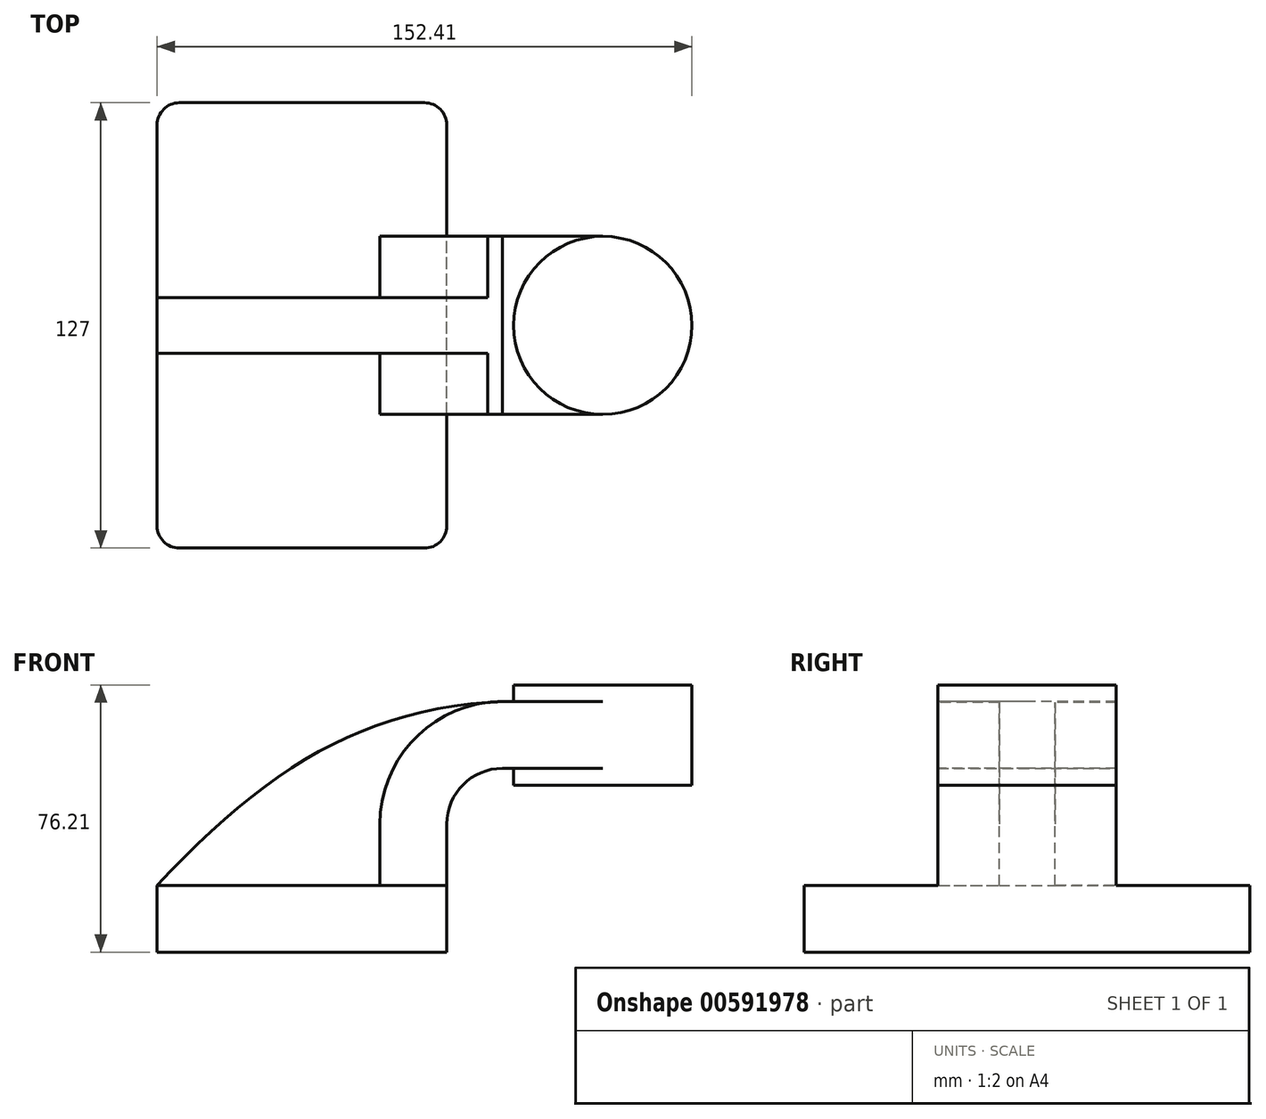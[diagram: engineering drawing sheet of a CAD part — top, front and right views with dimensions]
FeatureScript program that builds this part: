
annotation { "Feature Type Name" : "Feature", "Feature Type Description" : "" }
export const myFeature = defineFeature(function(context is Context, id is Id, definition is map)
    precondition{}
    {
        {
            var Q0;
            Q0=qCreatedBy(makeId("Front.planeOp"),FACE);
            var sketch = newSketch(context, id + "F0", { "sketchPlane" : qUnion([Q0])});
            skLineSegment(sketch, "E0.bottom", {"start": v(-41.28, -9.53) * mm, "end": v(41.28, -9.53) * mm});
            skLineSegment(sketch, "E0.top", {"start": v(-41.28, 9.52) * mm, "end": v(41.28, 9.52) * mm});
            skLineSegment(sketch, "E0.left", {"start": v(-41.28, -9.53) * mm, "end": v(-41.28, 9.52) * mm});
            skLineSegment(sketch, "E0.right", {"start": v(41.28, -9.53) * mm, "end": v(41.28, 9.52) * mm});
            skPoint(sketch, "E0.middle", {"position": v(0, 0) * mm});
            skLineSegment(sketch, "E1.bottom", {"start": v(111.12, 38.1) * mm, "end": v(60.32, 38.1) * mm});
            skLineSegment(sketch, "E1.top", {"start": v(111.12, 66.68) * mm, "end": v(60.32, 66.68) * mm});
            skLineSegment(sketch, "E1.left", {"start": v(111.12, 38.1) * mm, "end": v(111.12, 66.68) * mm});
            skLineSegment(sketch, "E1.right", {"start": v(60.32, 38.1) * mm, "end": v(60.32, 66.68) * mm});
            skPoint(sketch, "E1.middle", {"position": v(85.72, 52.39) * mm});
            skLineSegment(sketch, "E2", {"start": v(41.28, 9.52) * mm, "end": v(41.28, 27) * mm});
            skArc(sketch, "E3", {"start": v(41.28, 27) * mm, "mid": v(45.92, 38.23) * mm, "end": v(57.15, 42.88) * mm});
            skLineSegment(sketch, "E4", {"start": v(57.15, 42.88) * mm, "end": v(85.72, 42.88) * mm});
            skPoint(sketch, "E4.endSnap0", {"position": v(85.72, 38.1) * mm});
            skLineSegment(sketch, "E5.0", {"start": v(57.15, 61.93) * mm, "end": v(85.72, 61.93) * mm});
            skArc(sketch, "E5.1", {"start": v(22.23, 27) * mm, "mid": v(32.45, 51.7) * mm, "end": v(57.15, 61.93) * mm});
            skLineSegment(sketch, "E5.2", {"start": v(22.23, 9.52) * mm, "end": v(22.23, 27) * mm});
            skLineSegment(sketch, "E6", {"start": v(85.72, 38.1) * mm, "end": v(85.72, 66.68) * mm});
            skFitSpline(sketch, "E7", {"points": [v(-41.28, 9.53) * mm, v(57.15, 61.93) * mm], "startDerivative": vector(93.06, 99.37) * mm, "endDerivative": vector(120.58, 5.5) * mm});
            skSolve(sketch);
        }
        {
            var Q0;
            Q0=makeQuery(id+"F0.imprint","IMPRINT",FACE,{"disambiguationData":[TD([[makeQuery(id+"F0.imprint","IMPRINT",EDGE,{"derivedFrom":sQuery(id+"F0.wireOp",EDGE,"E0.bottom")}),1.0]])]});
            extrude(context, id + "F1", {"entities" : qUnion([Q0]), "depth" : 63.5 * mm, "offsetDistance" : 25.4 * mm});
        }
        {
            var Q0;
            {var subQ0=sQuery(id+"F0.wireOp",EDGE,"E4");var subQ1=sQuery(id+"F0.wireOp",EDGE,"E1.right");var subQ2=makeQuery(id+"F0.imprint","INTERSECT",VERTEX,{"derivedFrom":[subQ1,subQ0]});Q0=makeQuery(id+"F0.imprint","IMPRINT",FACE,{"disambiguationData":[TD([[makeQuery(id+"F0.imprint","IMPRINT",EDGE,{"disambiguationData":[TD([[subQ2,-1.0]])],"derivedFrom":subQ1}),-1.0]])]});}
            var Q1;
            {var subQ1=sQuery(id+"F0.wireOp",EDGE,"E2");Q1=makeQuery(id+"F0.imprint","IMPRINT",FACE,{"disambiguationData":[TD([[makeQuery(id+"F0.imprint","IMPRINT",EDGE,{"derivedFrom":subQ1}),1.0]])]});}
            extrude(context, id + "F2", {"entities" : qUnion([Q0, Q1]), "operationType" : NewBodyOperationType.ADD, "depth" : 25.4 * mm, "offsetDistance" : 25.4 * mm});
        }
        {
            var Q0;
            {var subQ3=sQuery(id+"F0.wireOp",EDGE,"E5.2");Q0=makeQuery(id+"F0.imprint","IMPRINT",FACE,{"disambiguationData":[TD([[makeQuery(id+"F0.imprint","IMPRINT",EDGE,{"derivedFrom":subQ3}),1.0]])]});}
            extrude(context, id + "F3", {"entities" : qUnion([Q0]), "operationType" : NewBodyOperationType.ADD, "endBound" : BoundingType.SYMMETRIC, "depth" : 15.88 * mm, "offsetDistance" : 25.4 * mm});
        }
        {
            var Q0;
            {var subQ1=sQuery(id+"F0.wireOp",EDGE,"E2");Q0=makeQuery(id+"F0.imprint","IMPRINT",FACE,{"disambiguationData":[TD([[makeQuery(id+"F0.imprint","IMPRINT",EDGE,{"derivedFrom":subQ1}),1.0]])]});}
            var Q1;
            {var subQ0=sQuery(id+"F0.wireOp",EDGE,"E4");var subQ1=sQuery(id+"F0.wireOp",EDGE,"E1.right");var subQ2=makeQuery(id+"F0.imprint","INTERSECT",VERTEX,{"derivedFrom":[subQ1,subQ0]});Q1=makeQuery(id+"F0.imprint","IMPRINT",FACE,{"disambiguationData":[TD([[makeQuery(id+"F0.imprint","IMPRINT",EDGE,{"disambiguationData":[TD([[subQ2,-1.0]])],"derivedFrom":subQ1}),-1.0]])]});}
            extrude(context, id + "F4", {"entities" : qUnion([Q0, Q1]), "operationType" : NewBodyOperationType.ADD, "endBound" : BoundingType.SYMMETRIC, "depth" : 50.8 * mm, "offsetDistance" : 25.4 * mm});
        }
        {
            var Q0;
            Q0=makeQuery(id+"F0.imprint","IMPRINT",FACE,{"disambiguationData":[TD([[makeQuery(id+"F0.imprint","IMPRINT",EDGE,{"derivedFrom":sQuery(id+"F0.wireOp",EDGE,"E0.bottom")}),1.0]])]});
            extrude(context, id + "F5", {"entities" : qUnion([Q0]), "operationType" : NewBodyOperationType.ADD, "depth" : -63.5 * mm, "offsetDistance" : 25.4 * mm});
        }
        {
            var Q0;
            {var subQ0=sQuery(id+"F0.wireOp",EDGE,"E1.left");Q0=makeQuery(id+"F0.imprint","IMPRINT",FACE,{"disambiguationData":[TD([[makeQuery(id+"F0.imprint","IMPRINT",EDGE,{"derivedFrom":subQ0}),1.0]])]});}
            var Q1;
            Q1=sQuery(id+"F0.wireOp",EDGE,"E6");
            revolve(context, id + "F6", {"operationType" : NewBodyOperationType.ADD, "entities" : qUnion([Q0]), "axis" : qUnion([Q1]), "revolveType" : RevolveType.FULL});
        }
        {
            var Q0;
            Q0=makeQuery(id+"F1.opExtrude","CAP_EDGE",EDGE,{"disambiguationData":[OSD([sQuery(id+"F0.wireOp",EDGE,"E0.left")])],"isStart":false});
            var Q1;
            Q1=makeQuery(id+"F1.opExtrude","CAP_EDGE",EDGE,{"disambiguationData":[OSD([sQuery(id+"F0.wireOp",EDGE,"E0.right")])],"isStart":false});
            var Q2;
            Q2=makeQuery(id+"F5.opExtrude","CAP_EDGE",EDGE,{"disambiguationData":[OSD([sQuery(id+"F0.wireOp",EDGE,"E0.right")])],"isStart":false});
            var Q3;
            Q3=makeQuery(id+"F5.opExtrude","CAP_EDGE",EDGE,{"disambiguationData":[OSD([sQuery(id+"F0.wireOp",EDGE,"E0.left")])],"isStart":false});
            fillet(context, id + "F7", {"entities" : qUnion([Q0, Q1, Q2, Q3]), "radius" : 6.35 * mm, "tangentPropagation" : true, "allowEdgeOverflow" : false});
        }
    });
